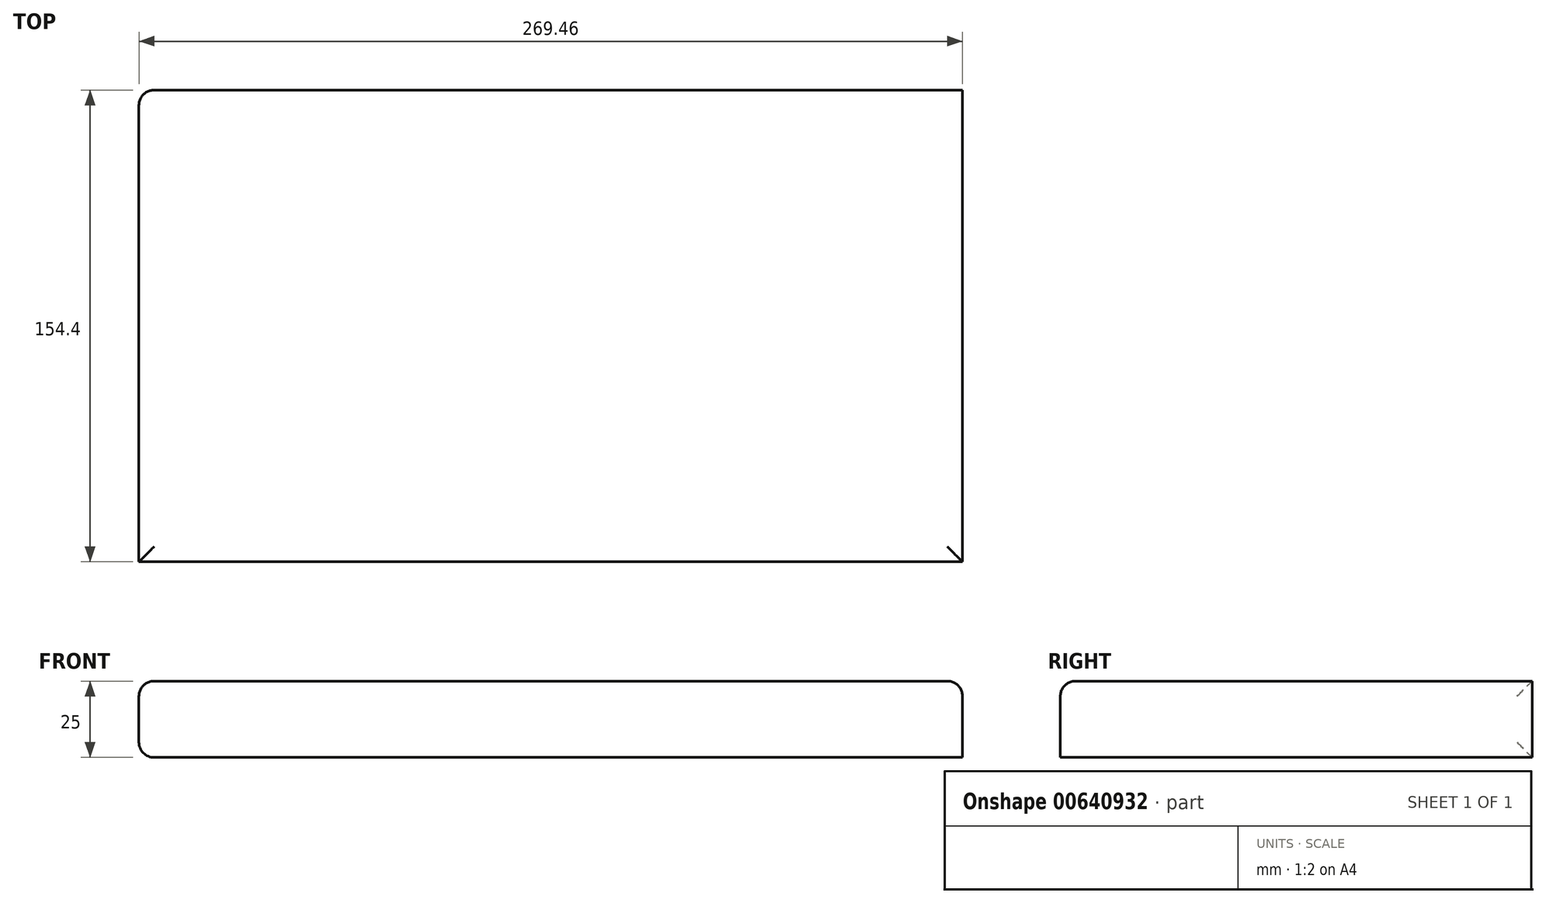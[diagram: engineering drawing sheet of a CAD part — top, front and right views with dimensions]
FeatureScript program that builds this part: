
annotation { "Feature Type Name" : "Feature", "Feature Type Description" : "" }
export const myFeature = defineFeature(function(context is Context, id is Id, definition is map)
    precondition{}
    {
        {
            var Q0;
            Q0=qCreatedBy(makeId("Top.planeOp"),FACE);
            var sketch = newSketch(context, id + "F0", { "sketchPlane" : qUnion([Q0])});
            skLineSegment(sketch, "E0.bottom", {"start": v(-136.83, 74.55) * mm, "end": v(132.63, 74.55) * mm});
            skLineSegment(sketch, "E0.top", {"start": v(-136.83, -79.85) * mm, "end": v(132.63, -79.85) * mm});
            skLineSegment(sketch, "E0.left", {"start": v(-136.83, 74.55) * mm, "end": v(-136.83, -79.85) * mm});
            skLineSegment(sketch, "E0.right", {"start": v(132.63, 74.55) * mm, "end": v(132.63, -79.85) * mm});
            skSolve(sketch);
        }
        {
            var Q0;
            Q0=makeQuery(id+"F0.imprint","IMPRINT",FACE,{"disambiguationData":[TD([[makeQuery(id+"F0.imprint","IMPRINT",EDGE,{"derivedFrom":sQuery(id+"F0.wireOp",EDGE,"E0.bottom")}),-1.0]])]});
            extrude(context, id + "F1", {"entities" : qUnion([Q0]), "depth" : 25 * mm, "offsetDistance" : 25 * mm});
        }
        {
            var Q0;
            Q0=makeQuery(id+"F1.opExtrude","CAP_EDGE",EDGE,{"disambiguationData":[OSD([sQuery(id+"F0.wireOp",EDGE,"E0.top")])],"isStart":false});
            var Q1;
            Q1=makeQuery(id+"F1.opExtrude","CAP_EDGE",EDGE,{"disambiguationData":[OSD([sQuery(id+"F0.wireOp",EDGE,"E0.right")])],"isStart":false});
            var Q2;
            Q2=makeQuery(id+"F1.opExtrude","CAP_EDGE",EDGE,{"disambiguationData":[OSD([sQuery(id+"F0.wireOp",EDGE,"E0.left")])],"isStart":false});
            var Q3;
            Q3=makeQuery(id+"F1.opExtrude","CAP_EDGE",EDGE,{"disambiguationData":[OSD([sQuery(id+"F0.wireOp",EDGE,"E0.left")])],"isStart":true});
            var Q4;
            Q4=makeQuery(id+"F1.opExtrude","SWEPT_EDGE",EDGE,{"disambiguationData":[OSD([sQuery(id+"F0.wireOp",EDGE,"E0.bottom"),sQuery(id+"F0.wireOp",EDGE,"E0.left")])]});
            fillet(context, id + "F2", {"entities" : qUnion([Q0, Q1, Q2, Q3, Q4]), "radius" : 5 * mm, "tangentPropagation" : true, "allowEdgeOverflow" : false});
        }
    });
